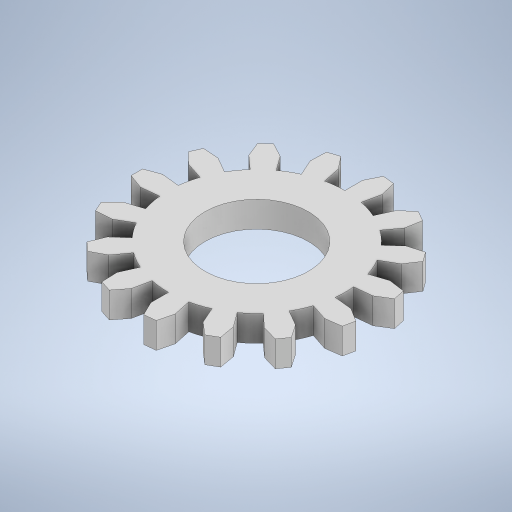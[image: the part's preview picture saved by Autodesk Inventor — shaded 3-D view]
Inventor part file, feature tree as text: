
AUTODESK INVENTOR PART (.ipt)
format: ipt  version: 2024.1 (Build 281209000, 209)  size: 390,656 bytes
history: native  units: mm
features: other x1, extrude x1, sketch x1
ambient origin geometry x8: Origin, YZ Plane, XZ Plane, XY Plane, X Axis, Y Axis, Z Axis, Center Point
bodies: Body1 (feature_tree)
feature tree (3):
  other  "ソリッド1"
  extrude  "押し出し1"  Depth=45.0mm
  sketch  "スケッチ1"
